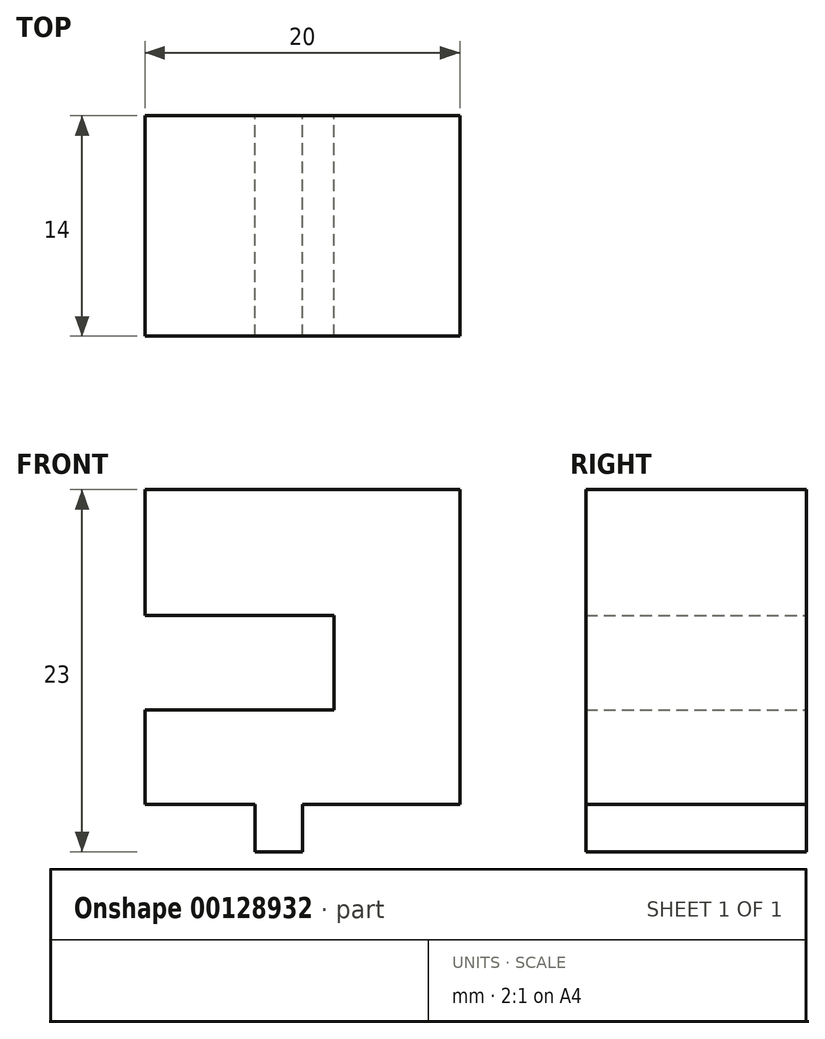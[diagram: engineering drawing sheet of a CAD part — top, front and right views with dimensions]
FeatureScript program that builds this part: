
annotation { "Feature Type Name" : "Feature", "Feature Type Description" : "" }
export const myFeature = defineFeature(function(context is Context, id is Id, definition is map)
    precondition{}
    {
        {
            var Q0;
            Q0=qCreatedBy(makeId("Front.planeOp"),FACE);
            var sketch = newSketch(context, id + "F0", { "sketchPlane" : qUnion([Q0])});
            skLineSegment(sketch, "E0", {"start": v(-13.92, -22.49) * mm, "end": v(-13.92, -16.49) * mm});
            skLineSegment(sketch, "E1", {"start": v(-13.92, -16.49) * mm, "end": v(-1.92, -16.49) * mm});
            skLineSegment(sketch, "E2", {"start": v(-1.92, -16.49) * mm, "end": v(-1.92, -10.49) * mm});
            skLineSegment(sketch, "E3", {"start": v(-1.92, -10.49) * mm, "end": v(-13.92, -10.49) * mm});
            skLineSegment(sketch, "E4", {"start": v(-13.92, -10.49) * mm, "end": v(-13.92, -2.49) * mm});
            skLineSegment(sketch, "E5", {"start": v(6.08, -2.49) * mm, "end": v(6.08, -22.49) * mm});
            skLineSegment(sketch, "E6", {"start": v(6.08, -2.49) * mm, "end": v(-13.92, -2.49) * mm});
            skLineSegment(sketch, "E7", {"start": v(-13.92, -22.49) * mm, "end": v(-6.92, -22.49) * mm});
            skLineSegment(sketch, "E8", {"start": v(-6.92, -22.49) * mm, "end": v(-6.92, -25.49) * mm});
            skLineSegment(sketch, "E9", {"start": v(-6.92, -25.49) * mm, "end": v(-3.92, -25.49) * mm});
            skLineSegment(sketch, "E10", {"start": v(-3.92, -25.49) * mm, "end": v(-3.92, -22.49) * mm});
            skLineSegment(sketch, "E11", {"start": v(-3.92, -22.49) * mm, "end": v(6.08, -22.49) * mm});
            skSolve(sketch);
        }
        {
            var Q0;
            Q0=makeQuery(id+"F0.imprint","IMPRINT",FACE,{"disambiguationData":[TD([[makeQuery(id+"F0.imprint","IMPRINT",EDGE,{"derivedFrom":sQuery(id+"F0.wireOp",EDGE,"E0")}),-1.0]])]});
            extrude(context, id + "F1", {"entities" : qUnion([Q0]), "depth" : 14 * mm});
        }
    });
